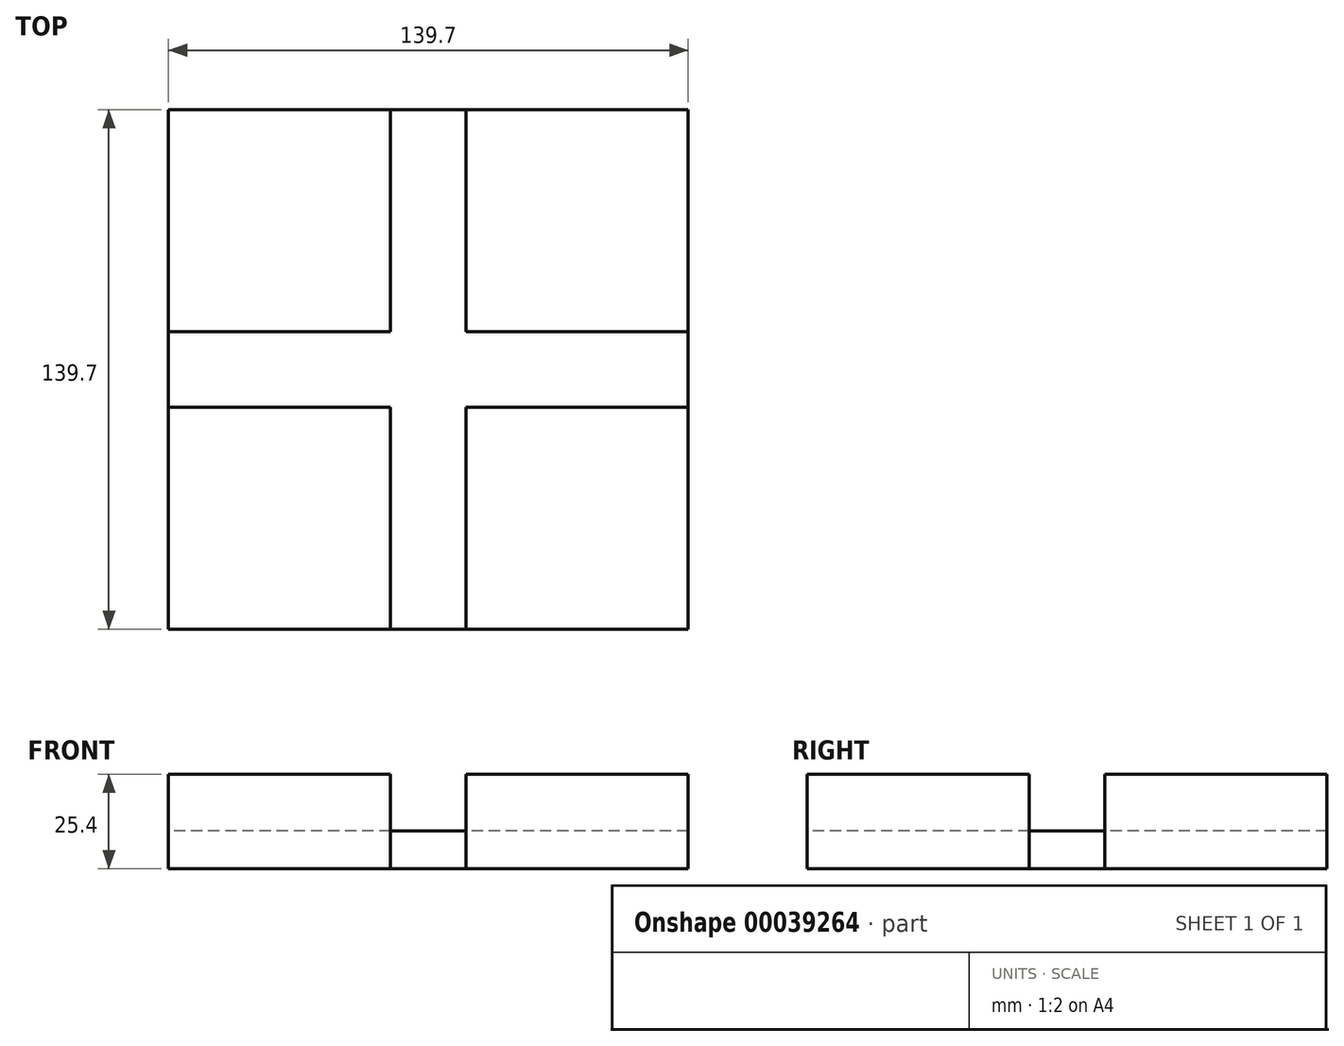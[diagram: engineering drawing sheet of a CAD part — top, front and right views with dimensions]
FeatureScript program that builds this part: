
annotation { "Feature Type Name" : "Feature", "Feature Type Description" : "" }
export const myFeature = defineFeature(function(context is Context, id is Id, definition is map)
    precondition{}
    {
        {
            var Q0;
            Q0=qCreatedBy(makeId("Top.planeOp"),FACE);
            var sketch = newSketch(context, id + "F0", { "sketchPlane" : qUnion([Q0])});
            skLineSegment(sketch, "E0.rect.bottom", {"start": v(69.85, 69.85) * mm, "end": v(-69.85, 69.85) * mm});
            skLineSegment(sketch, "E0.rect.top", {"start": v(69.85, -69.85) * mm, "end": v(-69.85, -69.85) * mm});
            skLineSegment(sketch, "E0.rect.left", {"start": v(69.85, 69.85) * mm, "end": v(69.85, -69.85) * mm});
            skLineSegment(sketch, "E0.rect.right", {"start": v(-69.85, 69.85) * mm, "end": v(-69.85, -69.85) * mm});
            skPoint(sketch, "E0.rect.middle", {"position": v(0, 0) * mm});
            skLineSegment(sketch, "E1.rect.left", {"start": v(10.16, 69.85) * mm, "end": v(10.16, 10.16) * mm});
            skLineSegment(sketch, "E1.rect.right", {"start": v(-10.16, 69.85) * mm, "end": v(-10.16, 10.16) * mm});
            skLineSegment(sketch, "E2.rect.bottom", {"start": v(69.85, 10.16) * mm, "end": v(10.16, 10.16) * mm});
            skLineSegment(sketch, "E2.rect.top", {"start": v(69.85, -10.16) * mm, "end": v(10.16, -10.16) * mm});
            skLineSegment(sketch, "E3.trimOffspring", {"start": v(-10.16, 10.16) * mm, "end": v(-69.85, 10.16) * mm});
            skLineSegment(sketch, "E4.trimOffspring", {"start": v(10.16, -10.16) * mm, "end": v(10.16, -69.85) * mm});
            skLineSegment(sketch, "E5.trimOffspring", {"start": v(-10.16, -10.16) * mm, "end": v(-69.85, -10.16) * mm});
            skLineSegment(sketch, "E6.trimOffspring", {"start": v(-10.16, -10.16) * mm, "end": v(-10.16, -69.85) * mm});
            skSolve(sketch);
        }
        {
            var Q0;
            {var subQ1=sQuery(id+"F0.wireOp",EDGE,"E1.rect.left");Q0=makeQuery(id+"F0.imprint","IMPRINT",FACE,{"disambiguationData":[TD([[makeQuery(id+"F0.imprint","IMPRINT",EDGE,{"derivedFrom":subQ1}),1.0]])]});}
            var Q1;
            {var subQ0=sQuery(id+"F0.wireOp",EDGE,"E2.rect.top");Q1=makeQuery(id+"F0.imprint","IMPRINT",FACE,{"disambiguationData":[TD([[makeQuery(id+"F0.imprint","IMPRINT",EDGE,{"derivedFrom":subQ0}),1.0]])]});}
            var Q2;
            {var subQ0=sQuery(id+"F0.wireOp",EDGE,"E5.trimOffspring");Q2=makeQuery(id+"F0.imprint","IMPRINT",FACE,{"disambiguationData":[TD([[makeQuery(id+"F0.imprint","IMPRINT",EDGE,{"derivedFrom":subQ0}),1.0]])]});}
            var Q3;
            {var subQ0=sQuery(id+"F0.wireOp",EDGE,"E1.rect.right");Q3=makeQuery(id+"F0.imprint","IMPRINT",FACE,{"disambiguationData":[TD([[makeQuery(id+"F0.imprint","IMPRINT",EDGE,{"derivedFrom":subQ0}),-1.0]])]});}
            extrude(context, id + "F1", {"entities" : qUnion([Q0, Q1, Q2, Q3]), "depth" : 25.4 * mm});
        }
        {
            var Q0;
            Q0=qCreatedBy(makeId("Top.planeOp"),FACE);
            var sketch = newSketch(context, id + "F2", { "sketchPlane" : qUnion([Q0])});
            skLineSegment(sketch, "E7.0", {"start": v(-10.16, 69.85) * mm, "end": v(-10.16, 10.16) * mm});
            skLineSegment(sketch, "E8.0", {"start": v(10.16, 69.85) * mm, "end": v(10.16, 10.16) * mm});
            skLineSegment(sketch, "E9.0", {"start": v(-10.16, 10.16) * mm, "end": v(-69.85, 10.16) * mm});
            skLineSegment(sketch, "E10.0", {"start": v(-10.16, -10.16) * mm, "end": v(-69.85, -10.16) * mm});
            skLineSegment(sketch, "E11.0", {"start": v(-10.16, -10.16) * mm, "end": v(-10.16, -69.85) * mm});
            skLineSegment(sketch, "E12.0", {"start": v(10.16, -10.16) * mm, "end": v(10.16, -69.85) * mm});
            skLineSegment(sketch, "E13.0", {"start": v(69.85, -10.16) * mm, "end": v(10.16, -10.16) * mm});
            skLineSegment(sketch, "E14.0", {"start": v(69.85, 10.16) * mm, "end": v(10.16, 10.16) * mm});
            skLineSegment(sketch, "E15", {"start": v(-69.85, 10.16) * mm, "end": v(-69.85, -10.16) * mm});
            skLineSegment(sketch, "E16", {"start": v(-10.16, 69.85) * mm, "end": v(10.16, 69.85) * mm});
            skLineSegment(sketch, "E17", {"start": v(69.85, -10.16) * mm, "end": v(69.85, 10.16) * mm});
            skLineSegment(sketch, "E18", {"start": v(10.16, -69.85) * mm, "end": v(-10.16, -69.85) * mm});
            skSolve(sketch);
        }
        {
            var Q0;
            Q0 = qSketchRegion(id + "F2", true);
            extrude(context, id + "F3", {"entities" : qUnion([Q0]), "depth" : 10.16 * mm});
        }
    });
